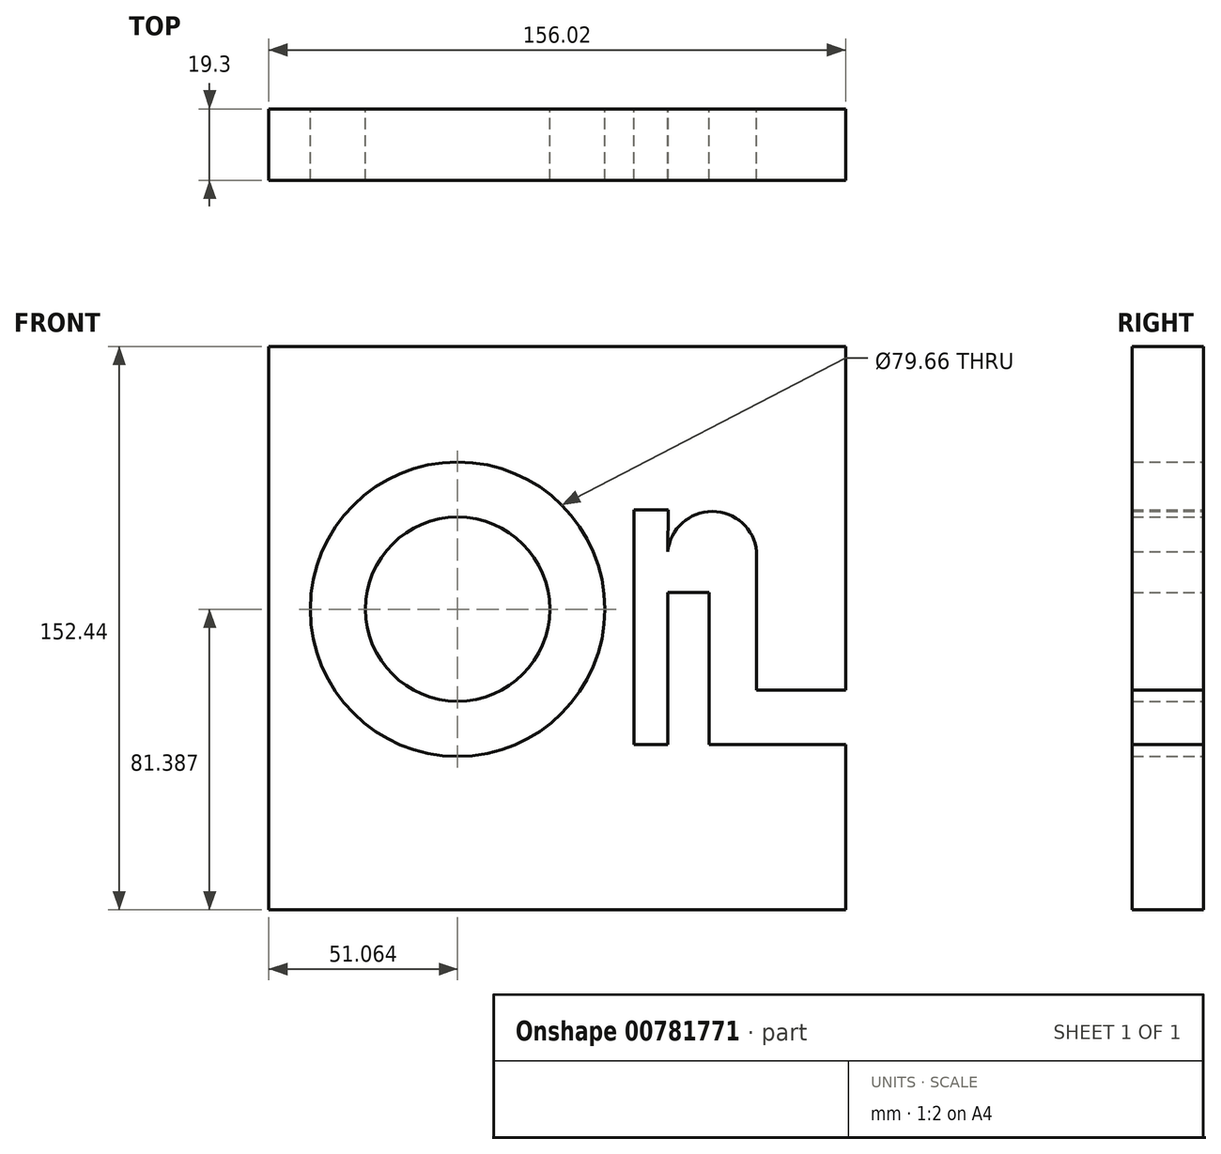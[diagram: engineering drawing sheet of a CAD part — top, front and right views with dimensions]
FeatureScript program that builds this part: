
annotation { "Feature Type Name" : "Feature", "Feature Type Description" : "" }
export const myFeature = defineFeature(function(context is Context, id is Id, definition is map)
    precondition{}
    {
        {
            var Q0;
            Q0=qCreatedBy(makeId("Front.planeOp"),FACE);
            var sketch = newSketch(context, id + "F0", { "sketchPlane" : qUnion([Q0])});
            skLineSegment(sketch, "E0.bottom", {"start": v(78, 76.22) * mm, "end": v(-78, 76.22) * mm});
            skLineSegment(sketch, "E0.top", {"start": v(78, -76.22) * mm, "end": v(-78, -76.22) * mm});
            skLineSegment(sketch, "E0.left", {"start": v(78, 76.22) * mm, "end": v(78, -76.22) * mm});
            skLineSegment(sketch, "E0.right", {"start": v(-78, 76.22) * mm, "end": v(-78, -76.22) * mm});
            skPoint(sketch, "E0.middle", {"position": v(0, 0) * mm});
            skCircle(sketch, "E1", {"center": v(-26.95, 5.17) * mm, "radius": 39.83 * mm});
            skCircle(sketch, "E2", {"center": v(-26.95, 5.17) * mm, "radius": 24.93 * mm});
            skLineSegment(sketch, "E3", {"start": v(20.82, 32.07) * mm, "end": v(20.82, -31.44) * mm});
            skLineSegment(sketch, "E4", {"start": v(20.82, -31.44) * mm, "end": v(29.92, -31.44) * mm});
            skLineSegment(sketch, "E5", {"start": v(29.92, -31.44) * mm, "end": v(29.92, 9.7) * mm});
            skLineSegment(sketch, "E6", {"start": v(29.92, 9.7) * mm, "end": v(41.05, 9.7) * mm});
            skLineSegment(sketch, "E7", {"start": v(41.05, 9.7) * mm, "end": v(41.05, -31.44) * mm});
            skLineSegment(sketch, "E8", {"start": v(41.05, -31.44) * mm, "end": v(78, -31.44) * mm});
            skLineSegment(sketch, "E9", {"start": v(78, -16.75) * mm, "end": v(53.98, -16.75) * mm});
            skLineSegment(sketch, "E10", {"start": v(53.98, -16.75) * mm, "end": v(53.98, 20.74) * mm});
            skArc(sketch, "E11", {"start": v(53.98, 20.74) * mm, "mid": v(41.95, 31.6) * mm, "end": v(29.92, 20.74) * mm});
            skLineSegment(sketch, "E12", {"start": v(20.82, 32.07) * mm, "end": v(30.1, 32.07) * mm});
            skLineSegment(sketch, "E13", {"start": v(29.92, 20.74) * mm, "end": v(30.1, 32.07) * mm});
            skSolve(sketch);
        }
        {
            var Q0;
            {var subQ0=sQuery(id+"F0.wireOp",EDGE,"E0.bottom");Q0=makeQuery(id+"F0.imprint","IMPRINT",FACE,{"disambiguationData":[TD([[makeQuery(id+"F0.imprint","IMPRINT",EDGE,{"derivedFrom":subQ0}),1.0]])]});}
            extrude(context, id + "F1", {"entities" : qUnion([Q0]), "endBound" : BoundingType.SYMMETRIC, "depth" : 19.3 * mm, "offsetDistance" : 25.4 * mm});
        }
        {
            var Q0;
            Q0=makeQuery(id+"F0.imprint","IMPRINT",FACE,{"disambiguationData":[TD([[makeQuery(id+"F0.imprint","IMPRINT",EDGE,{"derivedFrom":sQuery(id+"F0.wireOp",EDGE,"E2")}),1.0]])]});
            extrude(context, id + "F2", {"entities" : qUnion([Q0]), "endBound" : BoundingType.SYMMETRIC, "depth" : 19.3 * mm, "offsetDistance" : 25.4 * mm});
        }
    });
